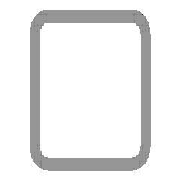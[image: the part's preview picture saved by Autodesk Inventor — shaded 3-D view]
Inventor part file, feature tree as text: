
AUTODESK INVENTOR PART (.ipt)
format: ipt  version: 2023.1 (Build 271208000, 208)  size: 149,504 bytes
history: native  units: mm (DEFAULTED — no unit token found)
features: other x4, plane x3, sketch x3, split x2
ambient origin geometry x8: Origin, YZ Plane, XZ Plane, XY Plane, X Axis, Y Axis, Z Axis, Center Point
bodies: Solid1 (feature_tree), Body (feature_tree)
feature tree (12):
  parser-record x1  (decoder bookkeeping rows leaked as tree rows — omitted from the tree; the rows remain in map.json)
  other  "Driven Length"
  other  "Start Plane"
  other  "End Plane"
  plane  "Work Plane4"
  split  "Split1"
  plane  "Work Plane5"
  split  "Split2"
  sketch  "Sketch"  dims[d10=50.8mm d11=50.8mm d12=3.175mm d13=-25.4mm d14=533.4mm d15=25.4mm d16=25.4mm d17=6.35mm d18=90.0deg d19=558.8mm]
  sketch  "Sketch3"  dims[d3=558.8mm]
  plane  "Work Plane3"
  sketch  "Sketch4"  dims[d4=0.0mm]
